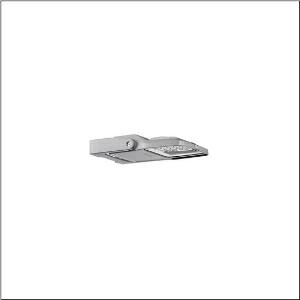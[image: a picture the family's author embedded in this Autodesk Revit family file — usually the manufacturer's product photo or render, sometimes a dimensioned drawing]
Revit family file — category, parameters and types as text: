
# Revit family: floodlight_fl_21_iq_micro___pl33t_5xa7761a4f2a_c8ff
name_source: partatom
category: Lighting Fixtures
units: mm (PartAtom-declared; Revit-internal decimal feet)

## family parameters
Cut with Voids When Loaded = No
Host = Face
Light Source = No
Part Type = Normal
Room Calculation Point = No
Round Connector Dimension = Use Diameter
Shared = No

## types (1)
- --- (1 x LED, 3050 lm, 23.1 W, 4000K)
    Apparent Load = 23 VA
    CIE Flux Codes = 26 75 99 100 100
    Color Rendering = 70
    Color Temperature = 4000K
    Default Elevation = 1800 mm
    Description = Floodlight FL 21 iQ micro, floodlight, primary light control with lens, of PMMA, primary optical cover: protective disc, of toughened safety glass, transparent, light distribution: PL33T, light emission: direct distribution, installation type: surface-mounted, LED, High Power LED, rated luminous flux: 3.050lm, luminous efficacy: 132lm/W, light colour: 740, colour temperature: 4000K, control: optimised constant luminous flux control (CLO 2.0), Desk-Remote (wireless, voltage-free reading and setting of iQ features in the workshop via application-optimized NFC function/RFID function), Light-Fading, Smart-Wire, Night-Set, Lumen-Switch, Temp-Guard, Auto-Match, with terminal, 6-pole, mains connection: 220..240V, AC, 50/60Hz, start of lifetime: 23W, end of service life: 24W, reduction: 11W, luminaire housing, of diecast aluminium, powder-coated, Siteco® metallic grey (DB 702S), corrosivity category C5 mid according to DIN EN ISO 12944, sealing non-destructively replaceable, design bracket, of diecast aluminium, powder-coated, Siteco® metallic grey (DB 702S), protection rating (complete): IP66, insulation class (complete): insulation class II (safety insulation), certification: CE, ENEC, VDE, protection symbol: D, impact resistance: IK07, permissible operating ambient temperature: -40..+40°C, permissible operating ambient temperature for outdoor applications: -40..+50°C, standard: DIN EN 12944, LABS conformity tested according to VDMA 24364:2018-05, packaging unit: 1 piece

Light Distribution: PL33T
    Height = 65 mm
    Lamp = 1 x LED
    Lamp Light Flux = 3050 lm
    Lamp Power = 23.1 W
    Lamp count = 1
    Length = 312 mm
    Luminous efficacy = 132 lm/W
    Manufacturer = Siteco
    ModVariant = No
    Model = 5XA7761A4F2A
    Mounting Place = Wall
    Mounting Type = Surface mounted
    Number of Poles = 1
    OnlyDefault = Yes
    Power Factor = 1
    Product Name = Floodlight FL 21 iQ micro | PL33T
    Product group = floodlight | wall mounted
    ProductGroupID = 2001
    Protection Class = Protection class II
    Protection Degree = IP 66
    RLX_Detail_Level = 1
    RLX_Emergency_Light_Flux = 0 lm
    RLX_Emergency_Type = 0
    RLX_Emergency_Type_DB = No
    RlxData = <blob elided: 97329 chars, md5=bef014b4>
    Socket = socket
    Standby Power = 0 W
    System Light Flux = 3050 lm
    System Power = 23 W
    Type Comments = factory setting: luminous flux: 100 % | dim-lin: 254 | 455 mA
    Type Image = l_1006878.jpg
    URL = http://relux.com
    VarID = @adj_098311
    Voltage = 0 V
    Weight = 0.00 kg
    Width = 230 mm

## geometry (parser evidence)
native form markers: Blend x4, Sweep x13
no freeform markers — native parametric forms only
